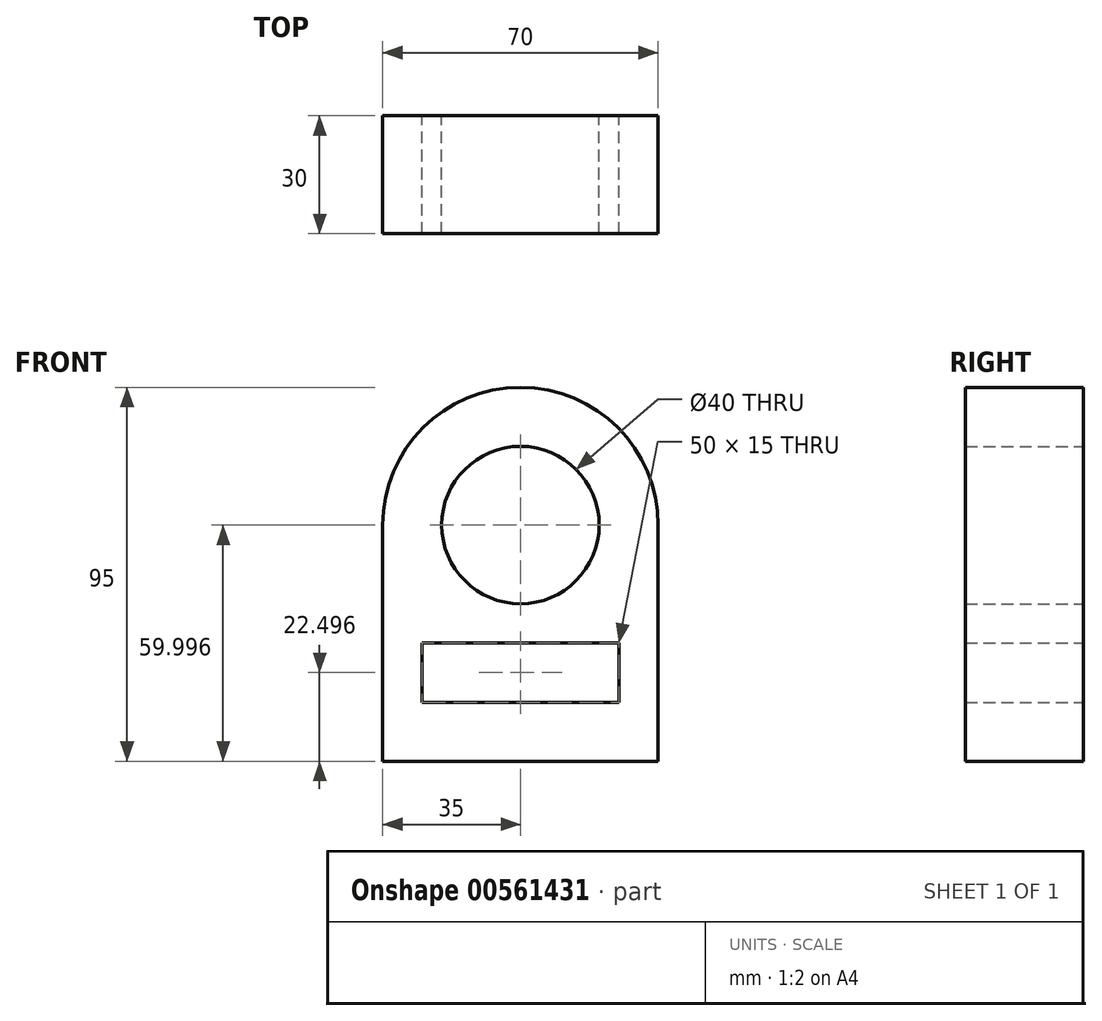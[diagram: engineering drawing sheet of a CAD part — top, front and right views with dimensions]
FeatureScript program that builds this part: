
annotation { "Feature Type Name" : "Feature", "Feature Type Description" : "" }
export const myFeature = defineFeature(function(context is Context, id is Id, definition is map)
    precondition{}
    {
        {
            var Q0;
            Q0=qCreatedBy(makeId("Front.planeOp"),FACE);
            var sketch = newSketch(context, id + "F0", { "sketchPlane" : qUnion([Q0])});
            skLineSegment(sketch, "E0", {"start": v(-25.8, -37.17) * mm, "end": v(44.2, -37.17) * mm});
            skLineSegment(sketch, "E1", {"start": v(44.2, -37.17) * mm, "end": v(44.2, 22.83) * mm});
            skLineSegment(sketch, "E2", {"start": v(-25.8, -37.17) * mm, "end": v(-25.8, 22.83) * mm});
            skLineSegment(sketch, "E3.bottom", {"start": v(-15.8, -7.17) * mm, "end": v(34.2, -7.17) * mm});
            skLineSegment(sketch, "E3.top", {"start": v(-15.8, -22.17) * mm, "end": v(34.2, -22.17) * mm});
            skLineSegment(sketch, "E3.left", {"start": v(-15.8, -7.17) * mm, "end": v(-15.8, -22.17) * mm});
            skLineSegment(sketch, "E3.right", {"start": v(34.2, -7.17) * mm, "end": v(34.2, -22.17) * mm});
            skCircle(sketch, "E4", {"center": v(9.2, 22.83) * mm, "radius": 20 * mm});
            skPoint(sketch, "E4.centerSnap0", {"position": v(9.2, -37.17) * mm});
            skArc(sketch, "E5", {"start": v(44.2, 22.83) * mm, "mid": v(9.2, 57.83) * mm, "end": v(-25.8, 22.83) * mm});
            skSolve(sketch);
        }
        {
            var Q0;
            Q0 = qSketchRegion(id + "F0", true);
            extrude(context, id + "F1", {"entities" : qUnion([Q0]), "depth" : 30 * mm, "offsetDistance" : 25 * mm});
        }
    });
